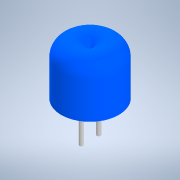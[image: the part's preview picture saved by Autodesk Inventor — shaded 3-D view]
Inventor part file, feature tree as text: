
AUTODESK INVENTOR PART (.ipt)
format: ipt  version: 2021 (Build 250183000, 183)  size: 154,624 bytes
history: native  units: mm
features: sketch x3, revolve x1, extrude x1
ambient origin geometry x8: Origin, YZ Plane, XZ Plane, XY Plane, X Axis, Y Axis, Z Axis, Center Point
bodies: Solid1 (feature_tree)
feature tree (5):
  revolve  "Revolution1"  [1 undecoded]
  sketch  "Sketch2"  dims[d2=4.0mm d3=90.0deg]
  sketch  "Sketch3"  dims[d4=1.0mm d5=1.0mm d6=10.0mm d7=0.0mm d8=4.835078mm]
  extrude  "Extrusion1"  TaperAngle=90.0deg  [1 undecoded]
  sketch  "Sketch1"  dims[d0=8.0mm d1=14.0mm]
note: 2 required parameter values undecoded (feature->parameter linkage not recoverable at this tier; creation-order binding heuristic only, values carry confidence <= 0.55)